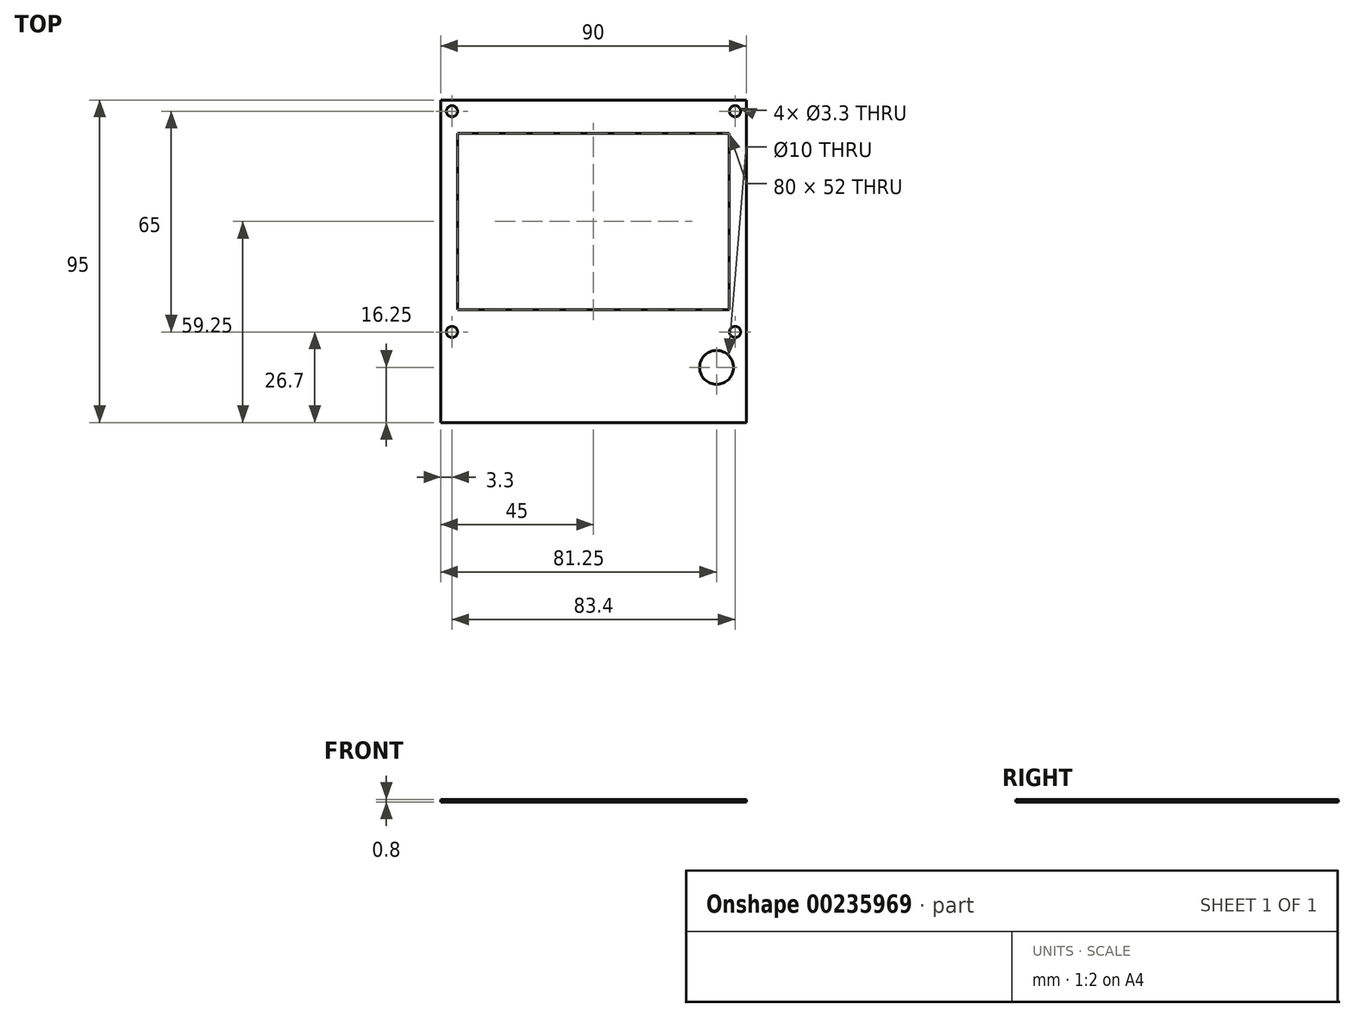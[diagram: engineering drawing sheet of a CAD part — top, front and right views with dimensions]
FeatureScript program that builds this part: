
annotation { "Feature Type Name" : "Feature", "Feature Type Description" : "" }
export const myFeature = defineFeature(function(context is Context, id is Id, definition is map)
    precondition{}
    {
        {
            var Q0;
            Q0=qCreatedBy(makeId("Top.planeOp"),FACE);
            var sketch = newSketch(context, id + "F0", { "sketchPlane" : qUnion([Q0])});
            skLineSegment(sketch, "E0.bottom", {"start": v(0, 0) * mm, "end": v(90, 0) * mm});
            skLineSegment(sketch, "E0.top", {"start": v(0, 95) * mm, "end": v(90, 95) * mm});
            skLineSegment(sketch, "E0.left", {"start": v(0, 0) * mm, "end": v(0, 95) * mm});
            skLineSegment(sketch, "E0.right", {"start": v(90, 0) * mm, "end": v(90, 95) * mm});
            skLineSegment(sketch, "E1.bottom", {"start": v(5, 85.25) * mm, "end": v(85, 85.25) * mm});
            skLineSegment(sketch, "E1.top", {"start": v(5, 33.25) * mm, "end": v(85, 33.25) * mm});
            skLineSegment(sketch, "E1.left", {"start": v(5, 85.25) * mm, "end": v(5, 33.25) * mm});
            skLineSegment(sketch, "E1.right", {"start": v(85, 85.25) * mm, "end": v(85, 33.25) * mm});
            skCircle(sketch, "E2", {"center": v(81.25, 16.25) * mm, "radius": 5 * mm});
            skCircle(sketch, "E3", {"center": v(3.3, 91.7) * mm, "radius": 1.65 * mm});
            skCircle(sketch, "E4", {"center": v(3.3, 26.7) * mm, "radius": 1.65 * mm});
            skCircle(sketch, "E5", {"center": v(86.7, 26.7) * mm, "radius": 1.65 * mm});
            skCircle(sketch, "E6", {"center": v(86.7, 91.7) * mm, "radius": 1.65 * mm});
            skSolve(sketch);
        }
        {
            var Q0;
            Q0 = qSketchRegion(id + "F0", true);
            extrude(context, id + "F1", {"entities" : qUnion([Q0]), "depth" : .8 * mm});
        }
    });
